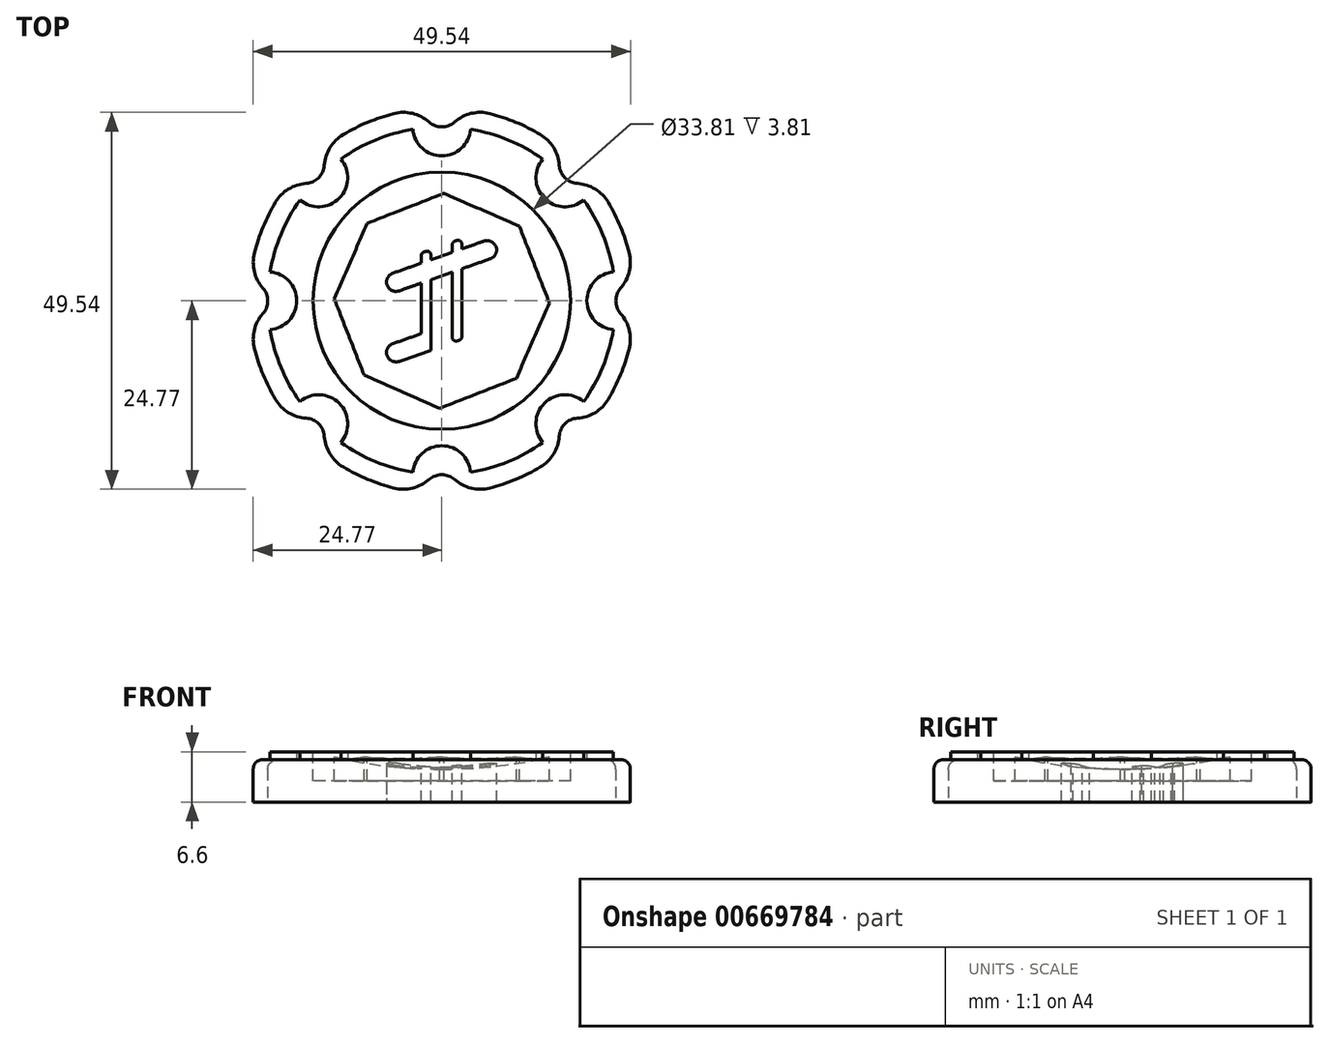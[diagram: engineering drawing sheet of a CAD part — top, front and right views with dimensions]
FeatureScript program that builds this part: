
annotation { "Feature Type Name" : "Feature", "Feature Type Description" : "" }
export const myFeature = defineFeature(function(context is Context, id is Id, definition is map)
    precondition{}
    {
        {
            var Q0;
            Q0=qCreatedBy(makeId("Top.planeOp"),FACE);
            var sketch = newSketch(context, id + "F0", { "sketchPlane" : qUnion([Q0])});
            skArc(sketch, "E0", {"start": v(-3.8, 22.54) * mm, "mid": v(-8.75, 21.12) * mm, "end": v(-13.26, 18.62) * mm});
            skArc(sketch, "E1", {"start": v(-2.54, 25.27) * mm, "mid": v(-9.72, 23.47) * mm, "end": v(-16.08, 19.66) * mm});
            skCircle(sketch, "E2", {"center": v(0, 0) * mm, "radius": 19.05 * mm});
            skArc(sketch, "E3", {"start": v(-2.54, 25.27) * mm, "mid": v(0, 22.86) * mm, "end": v(2.54, 25.27) * mm});
            skArc(sketch, "E4", {"start": v(-3.8, 22.54) * mm, "mid": v(0, 19.05) * mm, "end": v(3.8, 22.54) * mm});
            skArc(sketch, "E5.1.0", {"start": v(-18.62, 13.26) * mm, "mid": v(-13.47, 13.47) * mm, "end": v(-13.26, 18.62) * mm});
            skArc(sketch, "E5.1.1", {"start": v(-19.66, 16.08) * mm, "mid": v(-16.16, 16.16) * mm, "end": v(-16.08, 19.66) * mm});
            skArc(sketch, "E5.2.0", {"start": v(-22.54, -3.8) * mm, "mid": v(-19.05, 0) * mm, "end": v(-22.54, 3.8) * mm});
            skArc(sketch, "E5.2.1", {"start": v(-25.27, -2.54) * mm, "mid": v(-22.86, 0) * mm, "end": v(-25.27, 2.54) * mm});
            skArc(sketch, "E5.3.0", {"start": v(-13.26, -18.62) * mm, "mid": v(-13.47, -13.47) * mm, "end": v(-18.62, -13.26) * mm});
            skArc(sketch, "E5.3.1", {"start": v(-16.08, -19.66) * mm, "mid": v(-16.16, -16.16) * mm, "end": v(-19.66, -16.08) * mm});
            skArc(sketch, "E5.4.0", {"start": v(3.8, -22.54) * mm, "mid": v(0, -19.05) * mm, "end": v(-3.8, -22.54) * mm});
            skArc(sketch, "E5.4.1", {"start": v(2.54, -25.27) * mm, "mid": v(0, -22.86) * mm, "end": v(-2.54, -25.27) * mm});
            skArc(sketch, "E5.5.0", {"start": v(18.62, -13.26) * mm, "mid": v(13.47, -13.47) * mm, "end": v(13.26, -18.62) * mm});
            skArc(sketch, "E5.5.1", {"start": v(19.66, -16.08) * mm, "mid": v(16.16, -16.16) * mm, "end": v(16.08, -19.66) * mm});
            skArc(sketch, "E5.6.0", {"start": v(22.54, 3.8) * mm, "mid": v(19.05, 0) * mm, "end": v(22.54, -3.8) * mm});
            skArc(sketch, "E5.6.1", {"start": v(25.27, 2.54) * mm, "mid": v(22.86, 0) * mm, "end": v(25.27, -2.54) * mm});
            skArc(sketch, "E5.7.0", {"start": v(13.26, 18.62) * mm, "mid": v(13.47, 13.47) * mm, "end": v(18.62, 13.26) * mm});
            skArc(sketch, "E5.7.1", {"start": v(16.08, 19.66) * mm, "mid": v(16.16, 16.16) * mm, "end": v(19.66, 16.08) * mm});
            skArc(sketch, "E6.trimOffspring", {"start": v(-19.66, 16.08) * mm, "mid": v(-23.47, 9.72) * mm, "end": v(-25.27, 2.54) * mm});
            skArc(sketch, "E7.trimOffspring", {"start": v(-18.62, 13.26) * mm, "mid": v(-21.12, 8.75) * mm, "end": v(-22.54, 3.8) * mm});
            skArc(sketch, "E8.trimOffspring", {"start": v(-25.27, -2.54) * mm, "mid": v(-23.47, -9.72) * mm, "end": v(-19.66, -16.08) * mm});
            skArc(sketch, "E9.trimOffspring", {"start": v(-22.54, -3.8) * mm, "mid": v(-21.12, -8.75) * mm, "end": v(-18.62, -13.26) * mm});
            skArc(sketch, "E10.trimOffspring", {"start": v(13.26, 18.62) * mm, "mid": v(8.75, 21.12) * mm, "end": v(3.8, 22.54) * mm});
            skArc(sketch, "E11.trimOffspring", {"start": v(16.08, 19.66) * mm, "mid": v(9.72, 23.47) * mm, "end": v(2.54, 25.27) * mm});
            skArc(sketch, "E12.trimOffspring", {"start": v(-16.08, -19.66) * mm, "mid": v(-9.72, -23.47) * mm, "end": v(-2.54, -25.27) * mm});
            skArc(sketch, "E13.trimOffspring", {"start": v(-13.26, -18.62) * mm, "mid": v(-8.75, -21.12) * mm, "end": v(-3.8, -22.54) * mm});
            skArc(sketch, "E14.trimOffspring", {"start": v(3.8, -22.54) * mm, "mid": v(8.75, -21.12) * mm, "end": v(13.26, -18.62) * mm});
            skArc(sketch, "E15.trimOffspring", {"start": v(2.54, -25.27) * mm, "mid": v(9.72, -23.47) * mm, "end": v(16.08, -19.66) * mm});
            skArc(sketch, "E16.trimOffspring", {"start": v(18.62, -13.26) * mm, "mid": v(21.12, -8.75) * mm, "end": v(22.54, -3.8) * mm});
            skArc(sketch, "E17.trimOffspring", {"start": v(19.66, -16.08) * mm, "mid": v(23.47, -9.72) * mm, "end": v(25.27, -2.54) * mm});
            skArc(sketch, "E18.trimOffspring", {"start": v(22.54, 3.8) * mm, "mid": v(21.12, 8.75) * mm, "end": v(18.62, 13.26) * mm});
            skArc(sketch, "E19.trimOffspring", {"start": v(25.27, 2.54) * mm, "mid": v(23.47, 9.72) * mm, "end": v(19.66, 16.08) * mm});
            skCircle(sketch, "E20", {"center": v(0, 0) * mm, "radius": 9.53 * mm});
            skSolve(sketch);
        }
        {
            var Q0;
            {var subQ15=sQuery(id+"F0.wireOp",EDGE,"E0");Q0=makeQuery(id+"F0.imprint","IMPRINT",FACE,{"disambiguationData":[TD([[makeQuery(id+"F0.imprint","IMPRINT",EDGE,{"derivedFrom":subQ15}),-1.0]])]});}
            extrude(context, id + "F1", {"entities" : qUnion([Q0]), "depth" : 5.6 * mm, "offsetDistance" : 25.4 * mm});
        }
        {
            var Q0;
            {var subQ5=sQuery(id+"F0.wireOp",EDGE,"E7.trimOffspring");Q0=makeQuery(id+"F0.imprint","IMPRINT",FACE,{"disambiguationData":[TD([[makeQuery(id+"F0.imprint","IMPRINT",EDGE,{"derivedFrom":subQ5}),1.0]])]});}
            var Q1;
            {var subQ0=sQuery(id+"F0.wireOp",EDGE,"E0");Q1=makeQuery(id+"F0.imprint","IMPRINT",FACE,{"disambiguationData":[TD([[makeQuery(id+"F0.imprint","IMPRINT",EDGE,{"derivedFrom":subQ0}),1.0]])]});}
            var Q2;
            {var subQ5=sQuery(id+"F0.wireOp",EDGE,"E10.trimOffspring");Q2=makeQuery(id+"F0.imprint","IMPRINT",FACE,{"disambiguationData":[TD([[makeQuery(id+"F0.imprint","IMPRINT",EDGE,{"derivedFrom":subQ5}),1.0]])]});}
            var Q3;
            {var subQ5=sQuery(id+"F0.wireOp",EDGE,"E18.trimOffspring");Q3=makeQuery(id+"F0.imprint","IMPRINT",FACE,{"disambiguationData":[TD([[makeQuery(id+"F0.imprint","IMPRINT",EDGE,{"derivedFrom":subQ5}),1.0]])]});}
            var Q4;
            {var subQ5=sQuery(id+"F0.wireOp",EDGE,"E16.trimOffspring");Q4=makeQuery(id+"F0.imprint","IMPRINT",FACE,{"disambiguationData":[TD([[makeQuery(id+"F0.imprint","IMPRINT",EDGE,{"derivedFrom":subQ5}),1.0]])]});}
            var Q5;
            {var subQ5=sQuery(id+"F0.wireOp",EDGE,"E14.trimOffspring");Q5=makeQuery(id+"F0.imprint","IMPRINT",FACE,{"disambiguationData":[TD([[makeQuery(id+"F0.imprint","IMPRINT",EDGE,{"derivedFrom":subQ5}),1.0]])]});}
            var Q6;
            {var subQ5=sQuery(id+"F0.wireOp",EDGE,"E13.trimOffspring");Q6=makeQuery(id+"F0.imprint","IMPRINT",FACE,{"disambiguationData":[TD([[makeQuery(id+"F0.imprint","IMPRINT",EDGE,{"derivedFrom":subQ5}),1.0]])]});}
            var Q7;
            {var subQ5=sQuery(id+"F0.wireOp",EDGE,"E9.trimOffspring");Q7=makeQuery(id+"F0.imprint","IMPRINT",FACE,{"disambiguationData":[TD([[makeQuery(id+"F0.imprint","IMPRINT",EDGE,{"derivedFrom":subQ5}),1.0]])]});}
            extrude(context, id + "F2", {"entities" : qUnion([Q0, Q1, Q2, Q3, Q4, Q5, Q6, Q7]), "depth" : 6.6 * mm, "offsetDistance" : 25.4 * mm});
        }
        {
            var Q0;
            Q0=qCreatedBy(makeId("Right.planeOp"),FACE);
            var sketch = newSketch(context, id + "F3", { "sketchPlane" : qUnion([Q0])});
            skArc(sketch, "E21", {"start": v(0, 131.31) * mm, "mid": v(-63.5, 67.81) * mm, "end": v(0, 4.31) * mm});
            skLineSegment(sketch, "E22", {"start": v(0, 140.33) * mm, "end": v(0, -116.96) * mm});
            skSolve(sketch);
        }
        {
            var Q0;
            Q0=makeQuery(id+"F0.imprint","IMPRINT",FACE,{"disambiguationData":[TD([[makeQuery(id+"F0.imprint","IMPRINT",EDGE,{"derivedFrom":sQuery(id+"F0.wireOp",EDGE,"E20")}),-1.0]])]});
            var Q1;
            Q1=makeQuery(id+"F0.imprint","IMPRINT",FACE,{"disambiguationData":[TD([[makeQuery(id+"F0.imprint","IMPRINT",EDGE,{"derivedFrom":sQuery(id+"F0.wireOp",EDGE,"E20")}),1.0]])]});
            extrude(context, id + "F4", {"entities" : qUnion([Q0, Q1]), "depth" : 6.6 * mm, "offsetDistance" : 25.4 * mm});
        }
        {
            var Q0;
            {var subQ0=sQuery(id+"F3.wireOp",EDGE,"E21");Q0=makeQuery(id+"F3.imprint","IMPRINT",FACE,{"disambiguationData":[TD([[makeQuery(id+"F3.imprint","IMPRINT",EDGE,{"derivedFrom":subQ0}),1.0]])]});}
            var Q1;
            Q1=sQuery(id+"F3.wireOp",EDGE,"E22");
            revolve(context, id + "F5", {"operationType" : NewBodyOperationType.REMOVE, "entities" : qUnion([Q0]), "axis" : qUnion([Q1]), "revolveType" : RevolveType.FULL, "oppositeDirection" : true});
        }
        {
            var Q0;
            Q0=makeQuery(id+"F1.opExtrude","SWEPT_EDGE",EDGE,{"disambiguationData":[OSD([sQuery(id+"F0.wireOp",EDGE,"E1"),sQuery(id+"F0.wireOp",EDGE,"E5.1.1")])]});
            var Q1;
            Q1=makeQuery(id+"F1.opExtrude","SWEPT_EDGE",EDGE,{"disambiguationData":[OSD([sQuery(id+"F0.wireOp",EDGE,"E5.1.1"),sQuery(id+"F0.wireOp",EDGE,"E6.trimOffspring")])]});
            var Q2;
            Q2=makeQuery(id+"F1.opExtrude","SWEPT_EDGE",EDGE,{"disambiguationData":[OSD([sQuery(id+"F0.wireOp",EDGE,"E5.2.1"),sQuery(id+"F0.wireOp",EDGE,"E6.trimOffspring")])]});
            var Q3;
            Q3=makeQuery(id+"F1.opExtrude","SWEPT_EDGE",EDGE,{"disambiguationData":[OSD([sQuery(id+"F0.wireOp",EDGE,"E5.2.1"),sQuery(id+"F0.wireOp",EDGE,"E8.trimOffspring")])]});
            var Q4;
            Q4=makeQuery(id+"F1.opExtrude","SWEPT_EDGE",EDGE,{"disambiguationData":[OSD([sQuery(id+"F0.wireOp",EDGE,"E5.3.1"),sQuery(id+"F0.wireOp",EDGE,"E8.trimOffspring")])]});
            var Q5;
            Q5=makeQuery(id+"F1.opExtrude","SWEPT_EDGE",EDGE,{"disambiguationData":[OSD([sQuery(id+"F0.wireOp",EDGE,"E5.3.1"),sQuery(id+"F0.wireOp",EDGE,"E12.trimOffspring")])]});
            var Q6;
            Q6=makeQuery(id+"F1.opExtrude","SWEPT_EDGE",EDGE,{"disambiguationData":[OSD([sQuery(id+"F0.wireOp",EDGE,"E5.4.1"),sQuery(id+"F0.wireOp",EDGE,"E12.trimOffspring")])]});
            var Q7;
            Q7=makeQuery(id+"F1.opExtrude","SWEPT_EDGE",EDGE,{"disambiguationData":[OSD([sQuery(id+"F0.wireOp",EDGE,"E5.4.1"),sQuery(id+"F0.wireOp",EDGE,"E15.trimOffspring")])]});
            var Q8;
            Q8=makeQuery(id+"F1.opExtrude","SWEPT_EDGE",EDGE,{"disambiguationData":[OSD([sQuery(id+"F0.wireOp",EDGE,"E5.5.1"),sQuery(id+"F0.wireOp",EDGE,"E15.trimOffspring")])]});
            var Q9;
            Q9=makeQuery(id+"F1.opExtrude","SWEPT_EDGE",EDGE,{"disambiguationData":[OSD([sQuery(id+"F0.wireOp",EDGE,"E5.5.1"),sQuery(id+"F0.wireOp",EDGE,"E17.trimOffspring")])]});
            var Q10;
            Q10=makeQuery(id+"F1.opExtrude","SWEPT_EDGE",EDGE,{"disambiguationData":[OSD([sQuery(id+"F0.wireOp",EDGE,"E5.6.1"),sQuery(id+"F0.wireOp",EDGE,"E17.trimOffspring")])]});
            var Q11;
            Q11=makeQuery(id+"F1.opExtrude","SWEPT_EDGE",EDGE,{"disambiguationData":[OSD([sQuery(id+"F0.wireOp",EDGE,"E5.6.1"),sQuery(id+"F0.wireOp",EDGE,"E19.trimOffspring")])]});
            var Q12;
            Q12=makeQuery(id+"F1.opExtrude","SWEPT_EDGE",EDGE,{"disambiguationData":[OSD([sQuery(id+"F0.wireOp",EDGE,"E5.7.1"),sQuery(id+"F0.wireOp",EDGE,"E19.trimOffspring")])]});
            var Q13;
            Q13=makeQuery(id+"F1.opExtrude","SWEPT_EDGE",EDGE,{"disambiguationData":[OSD([sQuery(id+"F0.wireOp",EDGE,"E5.7.1"),sQuery(id+"F0.wireOp",EDGE,"E11.trimOffspring")])]});
            var Q14;
            Q14=makeQuery(id+"F1.opExtrude","SWEPT_EDGE",EDGE,{"disambiguationData":[OSD([sQuery(id+"F0.wireOp",EDGE,"E1"),sQuery(id+"F0.wireOp",EDGE,"E3")])]});
            var Q15;
            Q15=makeQuery(id+"F1.opExtrude","SWEPT_EDGE",EDGE,{"disambiguationData":[OSD([sQuery(id+"F0.wireOp",EDGE,"E3"),sQuery(id+"F0.wireOp",EDGE,"E11.trimOffspring")])]});
            fillet(context, id + "F6", {"entities" : qUnion([Q0, Q1, Q2, Q3, Q4, Q5, Q6, Q7, Q8, Q9, Q10, Q11, Q12, Q13, Q14, Q15]), "radius" : 5.08 * mm, "tangentPropagation" : true, "allowEdgeOverflow" : false});
        }
        {
            var Q0;
            Q0=makeQuery(id+"F1.opExtrude","CAP_EDGE",EDGE,{"disambiguationData":[OSD([sQuery(id+"F0.wireOp",EDGE,"E6.trimOffspring")])],"isStart":false});
            var Q1;
            {var subQ0=sQuery(id+"F0.wireOp",EDGE,"E6.trimOffspring");var subQ1=sQuery(id+"F0.wireOp",EDGE,"E5.1.1");Q1=makeQuery(id+"F6.opFillet","BLEND_EDGE",EDGE,{"blendedFrom":[makeQuery(id+"F1.opExtrude","SWEPT_EDGE",EDGE,{"disambiguationData":[OSD([subQ1,subQ0])]}),makeQuery(id+"F1.opExtrude","CAP_FACE",FACE,{"disambiguationData":[OSD([sQuery(id+"F0.wireOp",EDGE,"E0"),sQuery(id+"F0.wireOp",EDGE,"E1"),sQuery(id+"F0.wireOp",EDGE,"E3"),sQuery(id+"F0.wireOp",EDGE,"E4"),sQuery(id+"F0.wireOp",EDGE,"E5.1.0"),subQ1,sQuery(id+"F0.wireOp",EDGE,"E5.2.0"),sQuery(id+"F0.wireOp",EDGE,"E5.2.1"),sQuery(id+"F0.wireOp",EDGE,"E5.3.0"),sQuery(id+"F0.wireOp",EDGE,"E5.3.1"),sQuery(id+"F0.wireOp",EDGE,"E5.4.0"),sQuery(id+"F0.wireOp",EDGE,"E5.4.1"),sQuery(id+"F0.wireOp",EDGE,"E5.5.0"),sQuery(id+"F0.wireOp",EDGE,"E5.5.1"),sQuery(id+"F0.wireOp",EDGE,"E5.6.0"),sQuery(id+"F0.wireOp",EDGE,"E5.6.1"),sQuery(id+"F0.wireOp",EDGE,"E5.7.0"),sQuery(id+"F0.wireOp",EDGE,"E5.7.1"),subQ0,sQuery(id+"F0.wireOp",EDGE,"E7.trimOffspring"),sQuery(id+"F0.wireOp",EDGE,"E8.trimOffspring"),sQuery(id+"F0.wireOp",EDGE,"E9.trimOffspring"),sQuery(id+"F0.wireOp",EDGE,"E10.trimOffspring"),sQuery(id+"F0.wireOp",EDGE,"E11.trimOffspring"),sQuery(id+"F0.wireOp",EDGE,"E12.trimOffspring"),sQuery(id+"F0.wireOp",EDGE,"E13.trimOffspring"),sQuery(id+"F0.wireOp",EDGE,"E14.trimOffspring"),sQuery(id+"F0.wireOp",EDGE,"E15.trimOffspring"),sQuery(id+"F0.wireOp",EDGE,"E16.trimOffspring"),sQuery(id+"F0.wireOp",EDGE,"E17.trimOffspring"),sQuery(id+"F0.wireOp",EDGE,"E18.trimOffspring"),sQuery(id+"F0.wireOp",EDGE,"E19.trimOffspring")])],"isStart":false})],"blendedInto":[makeQuery(id+"F1.opExtrude","CAP_FACE",FACE,{"disambiguationData":[OSD([sQuery(id+"F0.wireOp",EDGE,"E0"),sQuery(id+"F0.wireOp",EDGE,"E1"),sQuery(id+"F0.wireOp",EDGE,"E3"),sQuery(id+"F0.wireOp",EDGE,"E4"),sQuery(id+"F0.wireOp",EDGE,"E5.1.0"),subQ1,sQuery(id+"F0.wireOp",EDGE,"E5.2.0"),sQuery(id+"F0.wireOp",EDGE,"E5.2.1"),sQuery(id+"F0.wireOp",EDGE,"E5.3.0"),sQuery(id+"F0.wireOp",EDGE,"E5.3.1"),sQuery(id+"F0.wireOp",EDGE,"E5.4.0"),sQuery(id+"F0.wireOp",EDGE,"E5.4.1"),sQuery(id+"F0.wireOp",EDGE,"E5.5.0"),sQuery(id+"F0.wireOp",EDGE,"E5.5.1"),sQuery(id+"F0.wireOp",EDGE,"E5.6.0"),sQuery(id+"F0.wireOp",EDGE,"E5.6.1"),sQuery(id+"F0.wireOp",EDGE,"E5.7.0"),sQuery(id+"F0.wireOp",EDGE,"E5.7.1"),subQ0,sQuery(id+"F0.wireOp",EDGE,"E7.trimOffspring"),sQuery(id+"F0.wireOp",EDGE,"E8.trimOffspring"),sQuery(id+"F0.wireOp",EDGE,"E9.trimOffspring"),sQuery(id+"F0.wireOp",EDGE,"E10.trimOffspring"),sQuery(id+"F0.wireOp",EDGE,"E11.trimOffspring"),sQuery(id+"F0.wireOp",EDGE,"E12.trimOffspring"),sQuery(id+"F0.wireOp",EDGE,"E13.trimOffspring"),sQuery(id+"F0.wireOp",EDGE,"E14.trimOffspring"),sQuery(id+"F0.wireOp",EDGE,"E15.trimOffspring"),sQuery(id+"F0.wireOp",EDGE,"E16.trimOffspring"),sQuery(id+"F0.wireOp",EDGE,"E17.trimOffspring"),sQuery(id+"F0.wireOp",EDGE,"E18.trimOffspring"),sQuery(id+"F0.wireOp",EDGE,"E19.trimOffspring")])],"isStart":false})]});}
            fillet(context, id + "F7", {"entities" : qUnion([Q0, Q1]), "radius" : 1.27 * mm, "tangentPropagation" : true, "allowEdgeOverflow" : false});
        }
        {
            var Q0;
            Q0=makeQuery(id+"F1.opExtrude","SWEPT_BODY",BODY,{"disambiguationData":[OSD([sQuery(id+"F0.wireOp",EDGE,"E0"),sQuery(id+"F0.wireOp",EDGE,"E1"),sQuery(id+"F0.wireOp",EDGE,"E3"),sQuery(id+"F0.wireOp",EDGE,"E4"),sQuery(id+"F0.wireOp",EDGE,"E5.1.0"),sQuery(id+"F0.wireOp",EDGE,"E5.1.1"),sQuery(id+"F0.wireOp",EDGE,"E5.2.0"),sQuery(id+"F0.wireOp",EDGE,"E5.2.1"),sQuery(id+"F0.wireOp",EDGE,"E5.3.0"),sQuery(id+"F0.wireOp",EDGE,"E5.3.1"),sQuery(id+"F0.wireOp",EDGE,"E5.4.0"),sQuery(id+"F0.wireOp",EDGE,"E5.4.1"),sQuery(id+"F0.wireOp",EDGE,"E5.5.0"),sQuery(id+"F0.wireOp",EDGE,"E5.5.1"),sQuery(id+"F0.wireOp",EDGE,"E5.6.0"),sQuery(id+"F0.wireOp",EDGE,"E5.6.1"),sQuery(id+"F0.wireOp",EDGE,"E5.7.0"),sQuery(id+"F0.wireOp",EDGE,"E5.7.1"),sQuery(id+"F0.wireOp",EDGE,"E6.trimOffspring"),sQuery(id+"F0.wireOp",EDGE,"E7.trimOffspring"),sQuery(id+"F0.wireOp",EDGE,"E8.trimOffspring"),sQuery(id+"F0.wireOp",EDGE,"E9.trimOffspring"),sQuery(id+"F0.wireOp",EDGE,"E10.trimOffspring"),sQuery(id+"F0.wireOp",EDGE,"E11.trimOffspring"),sQuery(id+"F0.wireOp",EDGE,"E12.trimOffspring"),sQuery(id+"F0.wireOp",EDGE,"E13.trimOffspring"),sQuery(id+"F0.wireOp",EDGE,"E14.trimOffspring"),sQuery(id+"F0.wireOp",EDGE,"E15.trimOffspring"),sQuery(id+"F0.wireOp",EDGE,"E16.trimOffspring"),sQuery(id+"F0.wireOp",EDGE,"E17.trimOffspring"),sQuery(id+"F0.wireOp",EDGE,"E18.trimOffspring"),sQuery(id+"F0.wireOp",EDGE,"E19.trimOffspring")])]});
            var Q1;
            Q1=makeQuery(id+"F2.opExtrude","SWEPT_BODY",BODY,{"disambiguationData":[OSD([sQuery(id+"F0.wireOp",EDGE,"E2"),sQuery(id+"F0.wireOp",EDGE,"E4"),sQuery(id+"F0.wireOp",EDGE,"E5.7.0"),sQuery(id+"F0.wireOp",EDGE,"E10.trimOffspring")])]});
            var Q2;
            Q2=makeQuery(id+"F2.opExtrude","SWEPT_BODY",BODY,{"disambiguationData":[OSD([sQuery(id+"F0.wireOp",EDGE,"E2"),sQuery(id+"F0.wireOp",EDGE,"E5.3.0"),sQuery(id+"F0.wireOp",EDGE,"E5.4.0"),sQuery(id+"F0.wireOp",EDGE,"E13.trimOffspring")])]});
            var Q3;
            Q3=makeQuery(id+"F2.opExtrude","SWEPT_BODY",BODY,{"disambiguationData":[OSD([sQuery(id+"F0.wireOp",EDGE,"E2"),sQuery(id+"F0.wireOp",EDGE,"E5.4.0"),sQuery(id+"F0.wireOp",EDGE,"E5.5.0"),sQuery(id+"F0.wireOp",EDGE,"E14.trimOffspring")])]});
            var Q4;
            Q4=makeQuery(id+"F2.opExtrude","SWEPT_BODY",BODY,{"disambiguationData":[OSD([sQuery(id+"F0.wireOp",EDGE,"E2"),sQuery(id+"F0.wireOp",EDGE,"E5.1.0"),sQuery(id+"F0.wireOp",EDGE,"E5.2.0"),sQuery(id+"F0.wireOp",EDGE,"E7.trimOffspring")])]});
            var Q5;
            Q5=makeQuery(id+"F2.opExtrude","SWEPT_BODY",BODY,{"disambiguationData":[OSD([sQuery(id+"F0.wireOp",EDGE,"E2"),sQuery(id+"F0.wireOp",EDGE,"E5.6.0"),sQuery(id+"F0.wireOp",EDGE,"E5.7.0"),sQuery(id+"F0.wireOp",EDGE,"E18.trimOffspring")])]});
            var Q6;
            Q6=makeQuery(id+"F2.opExtrude","SWEPT_BODY",BODY,{"disambiguationData":[OSD([sQuery(id+"F0.wireOp",EDGE,"E2"),sQuery(id+"F0.wireOp",EDGE,"E5.5.0"),sQuery(id+"F0.wireOp",EDGE,"E5.6.0"),sQuery(id+"F0.wireOp",EDGE,"E16.trimOffspring")])]});
            var Q7;
            Q7=makeQuery(id+"F2.opExtrude","SWEPT_BODY",BODY,{"disambiguationData":[OSD([sQuery(id+"F0.wireOp",EDGE,"E2"),sQuery(id+"F0.wireOp",EDGE,"E5.2.0"),sQuery(id+"F0.wireOp",EDGE,"E5.3.0"),sQuery(id+"F0.wireOp",EDGE,"E9.trimOffspring")])]});
            var Q8;
            Q8=makeQuery(id+"F2.opExtrude","SWEPT_BODY",BODY,{"disambiguationData":[OSD([sQuery(id+"F0.wireOp",EDGE,"E0"),sQuery(id+"F0.wireOp",EDGE,"E2"),sQuery(id+"F0.wireOp",EDGE,"E4"),sQuery(id+"F0.wireOp",EDGE,"E5.1.0")])]});
            var Q9;
            Q9=makeQuery(id+"F4.opExtrude","SWEPT_BODY",BODY,{"disambiguationData":[OSD([sQuery(id+"F0.wireOp",EDGE,"E2")])]});
            booleanBodies(context, id + "F8", {"operationType" : BooleanOperationType.UNION, "tools" : qUnion([Q0, Q1, Q2, Q3, Q4, Q5, Q6, Q7, Q8, Q9])});
        }
        {
            var Q0;
            {var subQ0=sQuery(id+"F0.wireOp",EDGE,"E2");var subQ1=sQuery(id+"F0.wireOp",EDGE,"E5.6.0");var subQ2=sQuery(id+"F0.wireOp",EDGE,"E5.5.0");var subQ3=sQuery(id+"F0.wireOp",EDGE,"E5.4.0");var subQ4=sQuery(id+"F0.wireOp",EDGE,"E5.3.0");var subQ5=sQuery(id+"F0.wireOp",EDGE,"E5.2.0");var subQ6=sQuery(id+"F0.wireOp",EDGE,"E5.1.0");var subQ7=sQuery(id+"F0.wireOp",EDGE,"E5.7.0");var subQ8=sQuery(id+"F0.wireOp",EDGE,"E4");Q0=makeQuery(id+"F8.opBoolean","MERGE",FACE,{"derivedFrom":[makeQuery(id+"F2.opExtrude","CAP_FACE",FACE,{"disambiguationData":[OSD([sQuery(id+"F0.wireOp",EDGE,"E0"),subQ0,subQ8,subQ6])],"isStart":false}),makeQuery(id+"F2.opExtrude","CAP_FACE",FACE,{"disambiguationData":[OSD([subQ0,subQ1,subQ7,sQuery(id+"F0.wireOp",EDGE,"E18.trimOffspring")])],"isStart":false}),makeQuery(id+"F2.opExtrude","CAP_FACE",FACE,{"disambiguationData":[OSD([subQ0,subQ8,subQ7,sQuery(id+"F0.wireOp",EDGE,"E10.trimOffspring")])],"isStart":false}),makeQuery(id+"F2.opExtrude","CAP_FACE",FACE,{"disambiguationData":[OSD([subQ0,subQ6,subQ5,sQuery(id+"F0.wireOp",EDGE,"E7.trimOffspring")])],"isStart":false}),makeQuery(id+"F2.opExtrude","CAP_FACE",FACE,{"disambiguationData":[OSD([subQ0,subQ5,subQ4,sQuery(id+"F0.wireOp",EDGE,"E9.trimOffspring")])],"isStart":false}),makeQuery(id+"F2.opExtrude","CAP_FACE",FACE,{"disambiguationData":[OSD([subQ0,subQ4,subQ3,sQuery(id+"F0.wireOp",EDGE,"E13.trimOffspring")])],"isStart":false}),makeQuery(id+"F2.opExtrude","CAP_FACE",FACE,{"disambiguationData":[OSD([subQ0,subQ3,subQ2,sQuery(id+"F0.wireOp",EDGE,"E14.trimOffspring")])],"isStart":false}),makeQuery(id+"F2.opExtrude","CAP_FACE",FACE,{"disambiguationData":[OSD([subQ0,subQ2,subQ1,sQuery(id+"F0.wireOp",EDGE,"E16.trimOffspring")])],"isStart":false}),makeQuery(id+"F4.opExtrude","CAP_FACE",FACE,{"disambiguationData":[OSD([subQ0])],"isStart":false})]});}
            var sketch = newSketch(context, id + "F9", { "sketchPlane" : qUnion([Q0])});
            skLineSegment(sketch, "E23", {"start": v(-2.7, 6.29) * mm, "end": v(-2.7, 4.94) * mm});
            skLineSegment(sketch, "E24", {"start": v(-7.27, -8.55) * mm, "end": v(-1.43, -6.5) * mm});
            skLineSegment(sketch, "E25", {"start": v(2.64, -5.06) * mm, "end": v(2.64, 4.2) * mm});
            skLineSegment(sketch, "E26", {"start": v(-7.27, 3.33) * mm, "end": v(-2.7, 4.94) * mm});
            skLineSegment(sketch, "E27.0", {"start": v(-7.27, -5.93) * mm, "end": v(-2.7, -4.32) * mm});
            skLineSegment(sketch, "E28.0", {"start": v(-7.27, 0.72) * mm, "end": v(-2.7, 2.33) * mm});
            skLineSegment(sketch, "E29.0", {"start": v(-1.43, 6.74) * mm, "end": v(-1.43, 5.39) * mm});
            skLineSegment(sketch, "E30.0", {"start": v(1.37, -5.5) * mm, "end": v(1.37, 3.76) * mm});
            skLineSegment(sketch, "E31", {"start": v(-7.27, -8.55) * mm, "end": v(-7.27, -5.93) * mm});
            skLineSegment(sketch, "E32", {"start": v(7.2, 8.43) * mm, "end": v(7.2, 5.82) * mm});
            skPoint(sketch, "E33.orphan", {"position": v(7.63, 7.23) * mm});
            skLineSegment(sketch, "E34.0", {"start": v(-2.7, 6.29) * mm, "end": v(-1.43, 6.74) * mm});
            skLineSegment(sketch, "E35.trimOffspring", {"start": v(1.37, 7.72) * mm, "end": v(2.64, 8.17) * mm});
            skLineSegment(sketch, "E36.trimOffspring", {"start": v(2.64, 6.82) * mm, "end": v(7.2, 8.43) * mm});
            skLineSegment(sketch, "E37.trimOffspring", {"start": v(2.64, 4.2) * mm, "end": v(7.2, 5.82) * mm});
            skLineSegment(sketch, "E38.trimOffspring", {"start": v(2.64, 6.82) * mm, "end": v(2.64, 8.17) * mm});
            skLineSegment(sketch, "E39.trimOffspring", {"start": v(1.37, 6.37) * mm, "end": v(1.37, 7.72) * mm});
            skLineSegment(sketch, "E40.trimOffspring", {"start": v(-1.43, 2.77) * mm, "end": v(-1.43, -6.5) * mm});
            skLineSegment(sketch, "E41.trimOffspring", {"start": v(-1.43, 5.39) * mm, "end": v(1.37, 6.37) * mm});
            skLineSegment(sketch, "E42.trimOffspring", {"start": v(-2.7, 2.33) * mm, "end": v(-2.7, -4.32) * mm});
            skLineSegment(sketch, "E43.trimOffspring", {"start": v(-1.43, 2.77) * mm, "end": v(1.37, 3.76) * mm});
            skLineSegment(sketch, "E44.trimOffspring", {"start": v(1.37, -5.5) * mm, "end": v(2.64, -5.06) * mm});
            skLineSegment(sketch, "E45.trimOffspring", {"start": v(-7.27, 0.72) * mm, "end": v(-7.27, 3.33) * mm});
            skSolve(sketch);
        }
        {
            var Q0;
            Q0=makeQuery(id+"F9.imprint","IMPRINT",FACE,{"disambiguationData":[TD([[makeQuery(id+"F9.imprint","IMPRINT",EDGE,{"derivedFrom":sQuery(id+"F9.wireOp",EDGE,"E23")}),1.0]])]});
            extrude(context, id + "F10", {"entities" : qUnion([Q0]), "operationType" : NewBodyOperationType.REMOVE, "oppositeDirection" : true, "depth" : 25.4 * mm, "offsetDistance" : 25.4 * mm});
        }
        {
            var Q0;
            Q0=makeQuery(id+"F10.boolean.opBoolean","COPY",EDGE,{"derivedFrom":makeQuery(id+"F10.opExtrude","SWEPT_EDGE",EDGE,{"disambiguationData":[OSD([sQuery(id+"F9.wireOp",EDGE,"E26"),sQuery(id+"F9.wireOp",EDGE,"E45.trimOffspring")])]})});
            var Q1;
            Q1=makeQuery(id+"F10.boolean.opBoolean","COPY",EDGE,{"derivedFrom":makeQuery(id+"F10.opExtrude","SWEPT_EDGE",EDGE,{"disambiguationData":[OSD([sQuery(id+"F9.wireOp",EDGE,"E28.0"),sQuery(id+"F9.wireOp",EDGE,"E45.trimOffspring")])]})});
            var Q2;
            Q2=makeQuery(id+"F10.boolean.opBoolean","COPY",EDGE,{"derivedFrom":makeQuery(id+"F10.opExtrude","SWEPT_EDGE",EDGE,{"disambiguationData":[OSD([sQuery(id+"F9.wireOp",EDGE,"E32"),sQuery(id+"F9.wireOp",EDGE,"E37.trimOffspring")])]})});
            var Q3;
            Q3=makeQuery(id+"F10.boolean.opBoolean","COPY",EDGE,{"derivedFrom":makeQuery(id+"F10.opExtrude","SWEPT_EDGE",EDGE,{"disambiguationData":[OSD([sQuery(id+"F9.wireOp",EDGE,"E32"),sQuery(id+"F9.wireOp",EDGE,"E36.trimOffspring")])]})});
            var Q4;
            Q4=makeQuery(id+"F10.boolean.opBoolean","COPY",EDGE,{"derivedFrom":makeQuery(id+"F10.opExtrude","SWEPT_EDGE",EDGE,{"disambiguationData":[OSD([sQuery(id+"F9.wireOp",EDGE,"E27.0"),sQuery(id+"F9.wireOp",EDGE,"E31")])]})});
            var Q5;
            Q5=makeQuery(id+"F10.boolean.opBoolean","COPY",EDGE,{"derivedFrom":makeQuery(id+"F10.opExtrude","SWEPT_EDGE",EDGE,{"disambiguationData":[OSD([sQuery(id+"F9.wireOp",EDGE,"E24"),sQuery(id+"F9.wireOp",EDGE,"E31")])]})});
            fillet(context, id + "F11", {"entities" : qUnion([Q0, Q1, Q2, Q3, Q4, Q5]), "radius" : 1.27 * mm, "tangentPropagation" : true, "allowEdgeOverflow" : false});
        }
        {
            var Q0;
            Q0=makeQuery(id+"F10.boolean.opBoolean","COPY",EDGE,{"derivedFrom":makeQuery(id+"F10.opExtrude","SWEPT_EDGE",EDGE,{"disambiguationData":[OSD([sQuery(id+"F9.wireOp",EDGE,"E25"),sQuery(id+"F9.wireOp",EDGE,"E44.trimOffspring")])]})});
            var Q1;
            Q1=makeQuery(id+"F10.boolean.opBoolean","COPY",EDGE,{"derivedFrom":makeQuery(id+"F10.opExtrude","SWEPT_EDGE",EDGE,{"disambiguationData":[OSD([sQuery(id+"F9.wireOp",EDGE,"E30.0"),sQuery(id+"F9.wireOp",EDGE,"E44.trimOffspring")])]})});
            var Q2;
            Q2=makeQuery(id+"F10.boolean.opBoolean","COPY",EDGE,{"derivedFrom":makeQuery(id+"F10.opExtrude","SWEPT_EDGE",EDGE,{"disambiguationData":[OSD([sQuery(id+"F9.wireOp",EDGE,"E23"),sQuery(id+"F9.wireOp",EDGE,"E34.0")])]})});
            var Q3;
            Q3=makeQuery(id+"F10.boolean.opBoolean","COPY",EDGE,{"derivedFrom":makeQuery(id+"F10.opExtrude","SWEPT_EDGE",EDGE,{"disambiguationData":[OSD([sQuery(id+"F9.wireOp",EDGE,"E35.trimOffspring"),sQuery(id+"F9.wireOp",EDGE,"E39.trimOffspring")])]})});
            var Q4;
            Q4=makeQuery(id+"F10.boolean.opBoolean","COPY",EDGE,{"derivedFrom":makeQuery(id+"F10.opExtrude","SWEPT_EDGE",EDGE,{"disambiguationData":[OSD([sQuery(id+"F9.wireOp",EDGE,"E29.0"),sQuery(id+"F9.wireOp",EDGE,"E34.0")])]})});
            var Q5;
            Q5=makeQuery(id+"F10.boolean.opBoolean","COPY",EDGE,{"derivedFrom":makeQuery(id+"F10.opExtrude","SWEPT_EDGE",EDGE,{"disambiguationData":[OSD([sQuery(id+"F9.wireOp",EDGE,"E35.trimOffspring"),sQuery(id+"F9.wireOp",EDGE,"E38.trimOffspring")])]})});
            fillet(context, id + "F12", {"entities" : qUnion([Q0, Q1, Q2, Q3, Q4, Q5]), "radius" : 0.5 * mm, "tangentPropagation" : true, "allowEdgeOverflow" : false});
        }
        {
            var Q0;
            {var subQ0=sQuery(id+"F0.wireOp",EDGE,"E2");var subQ1=sQuery(id+"F0.wireOp",EDGE,"E5.6.0");var subQ2=sQuery(id+"F0.wireOp",EDGE,"E5.5.0");var subQ3=sQuery(id+"F0.wireOp",EDGE,"E5.4.0");var subQ4=sQuery(id+"F0.wireOp",EDGE,"E5.3.0");var subQ5=sQuery(id+"F0.wireOp",EDGE,"E5.2.0");var subQ6=sQuery(id+"F0.wireOp",EDGE,"E5.1.0");var subQ7=sQuery(id+"F0.wireOp",EDGE,"E5.7.0");var subQ8=sQuery(id+"F0.wireOp",EDGE,"E4");Q0=makeQuery(id+"F8.opBoolean","MERGE",FACE,{"derivedFrom":[makeQuery(id+"F2.opExtrude","CAP_FACE",FACE,{"disambiguationData":[OSD([sQuery(id+"F0.wireOp",EDGE,"E0"),subQ0,subQ8,subQ6])],"isStart":false}),makeQuery(id+"F2.opExtrude","CAP_FACE",FACE,{"disambiguationData":[OSD([subQ0,subQ1,subQ7,sQuery(id+"F0.wireOp",EDGE,"E18.trimOffspring")])],"isStart":false}),makeQuery(id+"F2.opExtrude","CAP_FACE",FACE,{"disambiguationData":[OSD([subQ0,subQ8,subQ7,sQuery(id+"F0.wireOp",EDGE,"E10.trimOffspring")])],"isStart":false}),makeQuery(id+"F2.opExtrude","CAP_FACE",FACE,{"disambiguationData":[OSD([subQ0,subQ6,subQ5,sQuery(id+"F0.wireOp",EDGE,"E7.trimOffspring")])],"isStart":false}),makeQuery(id+"F2.opExtrude","CAP_FACE",FACE,{"disambiguationData":[OSD([subQ0,subQ5,subQ4,sQuery(id+"F0.wireOp",EDGE,"E9.trimOffspring")])],"isStart":false}),makeQuery(id+"F2.opExtrude","CAP_FACE",FACE,{"disambiguationData":[OSD([subQ0,subQ4,subQ3,sQuery(id+"F0.wireOp",EDGE,"E13.trimOffspring")])],"isStart":false}),makeQuery(id+"F2.opExtrude","CAP_FACE",FACE,{"disambiguationData":[OSD([subQ0,subQ3,subQ2,sQuery(id+"F0.wireOp",EDGE,"E14.trimOffspring")])],"isStart":false}),makeQuery(id+"F2.opExtrude","CAP_FACE",FACE,{"disambiguationData":[OSD([subQ0,subQ2,subQ1,sQuery(id+"F0.wireOp",EDGE,"E16.trimOffspring")])],"isStart":false}),makeQuery(id+"F4.opExtrude","CAP_FACE",FACE,{"disambiguationData":[OSD([subQ0])],"isStart":false})]});}
            var sketch = newSketch(context, id + "F13", { "sketchPlane" : qUnion([Q0])});
            skCircle(sketch, "E46.cCircle", {"center": v(0, 0) * mm, "radius": 13.06 * mm, "construction": true});
            skLineSegment(sketch, "E46.0", {"start": v(-9.79, 10.2) * mm, "end": v(0.28, 14.13) * mm});
            skLineSegment(sketch, "E46.1", {"start": v(0.28, 14.13) * mm, "end": v(10.2, 9.79) * mm});
            skLineSegment(sketch, "E46.2", {"start": v(10.2, 9.79) * mm, "end": v(14.13, -0.28) * mm});
            skLineSegment(sketch, "E46.3", {"start": v(14.13, -0.28) * mm, "end": v(9.79, -10.2) * mm});
            skLineSegment(sketch, "E46.4", {"start": v(9.79, -10.2) * mm, "end": v(-0.28, -14.13) * mm});
            skLineSegment(sketch, "E46.5", {"start": v(-0.28, -14.13) * mm, "end": v(-10.2, -9.79) * mm});
            skLineSegment(sketch, "E46.6", {"start": v(-10.2, -9.79) * mm, "end": v(-14.13, 0.28) * mm});
            skLineSegment(sketch, "E46.7", {"start": v(-14.13, 0.28) * mm, "end": v(-9.79, 10.2) * mm});
            skPoint(sketch, "E46.0.midPoint", {"position": v(-4.75, 11.12) * mm});
            skSolve(sketch);
        }
        {
            var Q0;
            Q0=makeQuery(id+"F13.imprint","IMPRINT",FACE,{"disambiguationData":[TD([[makeQuery(id+"F13.imprint","IMPRINT",EDGE,{"derivedFrom":sQuery(id+"F13.wireOp",EDGE,"E46.0")}),1.0]])]});
            extrude(context, id + "F14", {"entities" : qUnion([Q0]), "operationType" : NewBodyOperationType.REMOVE, "oppositeDirection" : true, "depth" : 3.8 * mm, "offsetDistance" : 25.4 * mm});
        }
    });
